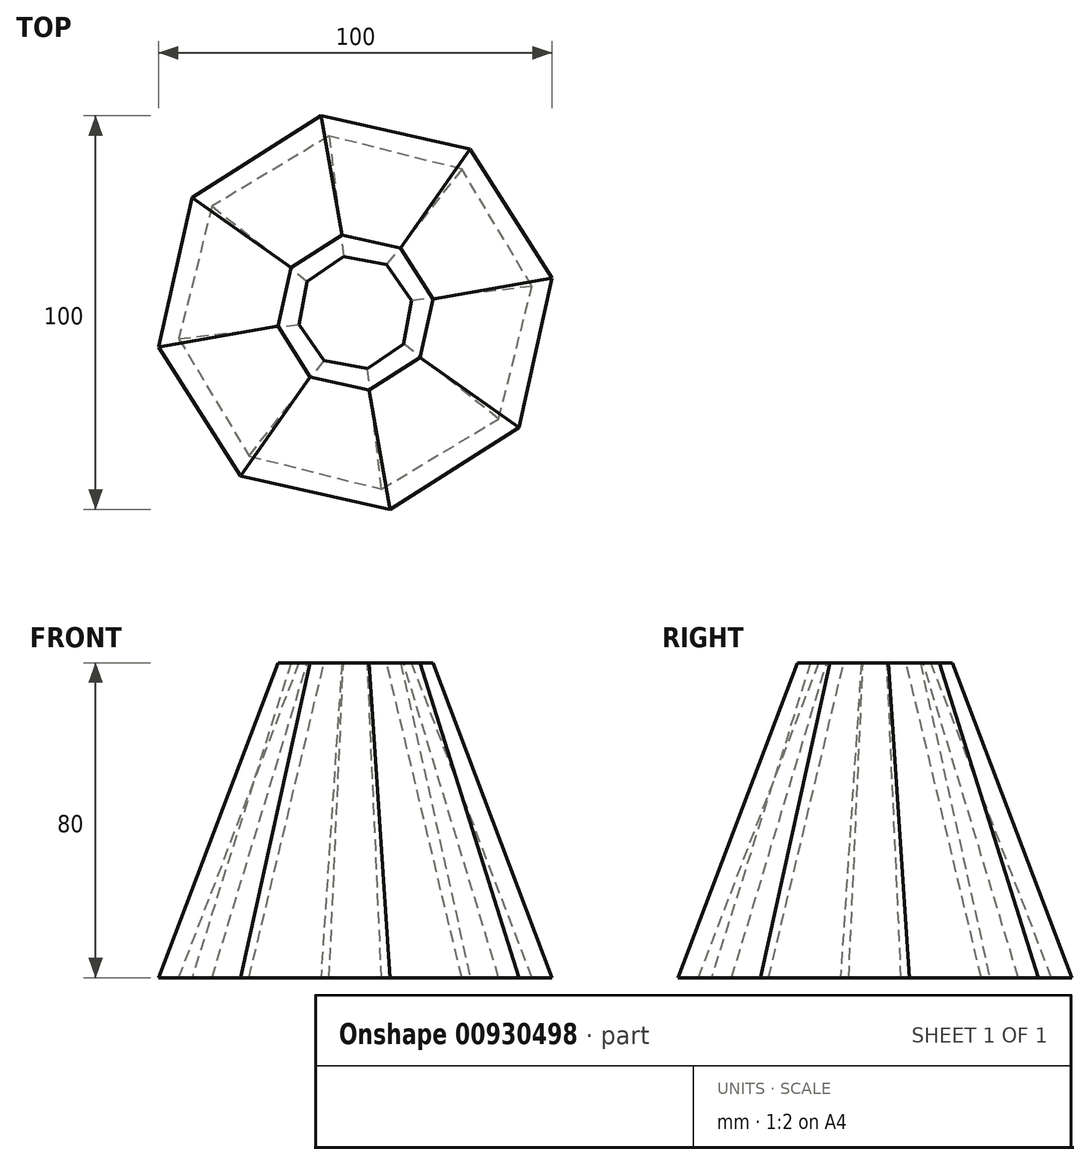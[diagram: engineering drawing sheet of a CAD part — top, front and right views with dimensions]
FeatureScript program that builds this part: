
annotation { "Feature Type Name" : "Feature", "Feature Type Description" : "" }
export const myFeature = defineFeature(function(context is Context, id is Id, definition is map)
    precondition{}
    {
        {
            var Q0;
            Q0=qCreatedBy(makeId("Top.planeOp"),FACE);
            var sketch = newSketch(context, id + "F0", { "sketchPlane" : qUnion([Q0])});
            skCircle(sketch, "E0.cCircle", {"center": v(0, 0) * mm, "radius": 46.9 * mm, "construction": true});
            skLineSegment(sketch, "E0.0", {"start": v(41.56, -29.15) * mm, "end": v(8.77, -50) * mm});
            skLineSegment(sketch, "E0.1", {"start": v(8.77, -50) * mm, "end": v(-29.15, -41.56) * mm});
            skLineSegment(sketch, "E0.2", {"start": v(-29.15, -41.56) * mm, "end": v(-50, -8.77) * mm});
            skLineSegment(sketch, "E0.3", {"start": v(-50, -8.77) * mm, "end": v(-41.56, 29.15) * mm});
            skLineSegment(sketch, "E0.4", {"start": v(-41.56, 29.15) * mm, "end": v(-8.77, 50) * mm});
            skLineSegment(sketch, "E0.5", {"start": v(-8.77, 50) * mm, "end": v(29.15, 41.56) * mm});
            skLineSegment(sketch, "E0.6", {"start": v(29.15, 41.56) * mm, "end": v(50, 8.77) * mm});
            skLineSegment(sketch, "E0.7", {"start": v(50, 8.77) * mm, "end": v(41.56, -29.15) * mm});
            skPoint(sketch, "E0.0.midPoint", {"position": v(25.16, -39.58) * mm});
            skPoint(sketch, "E1.0.midPoint", {"position": v(27.2, -39.24) * mm});
            skPoint(sketch, "E2.0.midPoint", {"position": v(4.46, -28.05) * mm});
            skCircle(sketch, "E3.cCircle", {"center": v(0, 0) * mm, "radius": 33.05 * mm, "construction": true});
            skLineSegment(sketch, "E3.0", {"start": v(29.09, -20.82) * mm, "end": v(5.85, -35.29) * mm});
            skLineSegment(sketch, "E3.1", {"start": v(5.85, -35.29) * mm, "end": v(-20.82, -29.09) * mm});
            skLineSegment(sketch, "E3.2", {"start": v(-20.82, -29.09) * mm, "end": v(-35.29, -5.85) * mm});
            skLineSegment(sketch, "E3.3", {"start": v(-35.29, -5.85) * mm, "end": v(-29.09, 20.82) * mm});
            skLineSegment(sketch, "E3.4", {"start": v(-29.09, 20.82) * mm, "end": v(-5.85, 35.29) * mm});
            skLineSegment(sketch, "E3.5", {"start": v(-5.85, 35.29) * mm, "end": v(20.82, 29.09) * mm});
            skLineSegment(sketch, "E3.6", {"start": v(20.82, 29.09) * mm, "end": v(35.29, 5.85) * mm});
            skLineSegment(sketch, "E3.7", {"start": v(35.29, 5.85) * mm, "end": v(29.09, -20.82) * mm});
            skPoint(sketch, "E3.0.midPoint", {"position": v(17.47, -28.05) * mm});
            skLineSegment(sketch, "E4", {"start": v(-8.77, 50) * mm, "end": v(-5.85, 35.29) * mm});
            skLineSegment(sketch, "E5", {"start": v(29.15, 41.56) * mm, "end": v(20.82, 29.09) * mm});
            skLineSegment(sketch, "E6", {"start": v(50, 8.77) * mm, "end": v(35.29, 5.85) * mm});
            skLineSegment(sketch, "E7", {"start": v(41.56, -29.15) * mm, "end": v(29.09, -20.82) * mm});
            skLineSegment(sketch, "E8", {"start": v(8.77, -50) * mm, "end": v(5.85, -35.29) * mm});
            skLineSegment(sketch, "E9", {"start": v(-29.15, -41.56) * mm, "end": v(-20.82, -29.09) * mm});
            skLineSegment(sketch, "E10", {"start": v(-50, -8.77) * mm, "end": v(-35.29, -5.85) * mm});
            skLineSegment(sketch, "E11", {"start": v(-41.56, 29.15) * mm, "end": v(-29.09, 20.82) * mm});
            skSolve(sketch);
        }
        {
            var Q0;
            Q0=makeQuery(id+"F0.imprint","IMPRINT",FACE,{"disambiguationData":[TD([[makeQuery(id+"F0.imprint","IMPRINT",EDGE,{"derivedFrom":sQuery(id+"F0.wireOp",EDGE,"E3.0")}),-1.0]])]});
            var Q1;
            Q1=makeQuery(id+"F0.imprint","IMPRINT",FACE,{"disambiguationData":[TD([[makeQuery(id+"F0.imprint","IMPRINT",EDGE,{"derivedFrom":sQuery(id+"F0.wireOp",EDGE,"E0.7")}),-1.0]])]});
            var Q2;
            Q2=makeQuery(id+"F0.imprint","IMPRINT",FACE,{"disambiguationData":[TD([[makeQuery(id+"F0.imprint","IMPRINT",EDGE,{"derivedFrom":sQuery(id+"F0.wireOp",EDGE,"E0.6")}),-1.0]])]});
            var Q3;
            Q3=makeQuery(id+"F0.imprint","IMPRINT",FACE,{"disambiguationData":[TD([[makeQuery(id+"F0.imprint","IMPRINT",EDGE,{"derivedFrom":sQuery(id+"F0.wireOp",EDGE,"E0.5")}),-1.0]])]});
            var Q4;
            Q4=makeQuery(id+"F0.imprint","IMPRINT",FACE,{"disambiguationData":[TD([[makeQuery(id+"F0.imprint","IMPRINT",EDGE,{"derivedFrom":sQuery(id+"F0.wireOp",EDGE,"E0.4")}),-1.0]])]});
            var Q5;
            Q5=makeQuery(id+"F0.imprint","IMPRINT",FACE,{"disambiguationData":[TD([[makeQuery(id+"F0.imprint","IMPRINT",EDGE,{"derivedFrom":sQuery(id+"F0.wireOp",EDGE,"E0.3")}),-1.0]])]});
            var Q6;
            Q6=makeQuery(id+"F0.imprint","IMPRINT",FACE,{"disambiguationData":[TD([[makeQuery(id+"F0.imprint","IMPRINT",EDGE,{"derivedFrom":sQuery(id+"F0.wireOp",EDGE,"E0.2")}),-1.0]])]});
            var Q7;
            Q7=makeQuery(id+"F0.imprint","IMPRINT",FACE,{"disambiguationData":[TD([[makeQuery(id+"F0.imprint","IMPRINT",EDGE,{"derivedFrom":sQuery(id+"F0.wireOp",EDGE,"E0.1")}),-1.0]])]});
            var Q8;
            Q8=makeQuery(id+"F0.imprint","IMPRINT",FACE,{"disambiguationData":[TD([[makeQuery(id+"F0.imprint","IMPRINT",EDGE,{"derivedFrom":sQuery(id+"F0.wireOp",EDGE,"E0.0")}),-1.0]])]});
            extrude(context, id + "F1", {"entities" : qUnion([Q0, Q1, Q2, Q3, Q4, Q5, Q6, Q7, Q8]), "depth" : 80 * mm, "offsetDistance" : 25 * mm});
        }
        {
            var Q0;
            Q0=makeQuery(id+"F1.opExtrude","CAP_FACE",FACE,{"disambiguationData":[OSD([sQuery(id+"F0.wireOp",EDGE,"E0.0"),sQuery(id+"F0.wireOp",EDGE,"E0.1"),sQuery(id+"F0.wireOp",EDGE,"E0.2"),sQuery(id+"F0.wireOp",EDGE,"E0.3"),sQuery(id+"F0.wireOp",EDGE,"E0.4"),sQuery(id+"F0.wireOp",EDGE,"E0.5"),sQuery(id+"F0.wireOp",EDGE,"E0.6"),sQuery(id+"F0.wireOp",EDGE,"E0.7")])],"isStart":false});
            var sketch = newSketch(context, id + "F2", { "sketchPlane" : qUnion([Q0])});
            skPoint(sketch, "E12.0.midPoint", {"position": v(11.44, -10.72) * mm});
            skCircle(sketch, "E13.cCircle", {"center": v(0, 0) * mm, "radius": 18.48 * mm, "construction": true});
            skLineSegment(sketch, "E13.0", {"start": v(16.37, -11.49) * mm, "end": v(3.46, -19.7) * mm});
            skLineSegment(sketch, "E13.1", {"start": v(3.46, -19.7) * mm, "end": v(-11.49, -16.37) * mm});
            skLineSegment(sketch, "E13.2", {"start": v(-11.49, -16.37) * mm, "end": v(-19.7, -3.46) * mm});
            skLineSegment(sketch, "E13.3", {"start": v(-19.7, -3.46) * mm, "end": v(-16.37, 11.49) * mm});
            skLineSegment(sketch, "E13.4", {"start": v(-16.37, 11.49) * mm, "end": v(-3.46, 19.7) * mm});
            skLineSegment(sketch, "E13.5", {"start": v(-3.46, 19.7) * mm, "end": v(11.49, 16.37) * mm});
            skLineSegment(sketch, "E13.6", {"start": v(11.49, 16.37) * mm, "end": v(19.7, 3.46) * mm});
            skLineSegment(sketch, "E13.7", {"start": v(19.7, 3.46) * mm, "end": v(16.37, -11.49) * mm});
            skPoint(sketch, "E13.0.midPoint", {"position": v(9.91, -15.6) * mm});
            skSolve(sketch);
        }
        {
            var Q1;
            Q1=makeQuery(id+"F2.imprint","IMPRINT",FACE,{"disambiguationData":[TD([[makeQuery(id+"F2.imprint","IMPRINT",EDGE,{"derivedFrom":sQuery(id+"F2.wireOp",EDGE,"E13.0")}),-1.0]])]});
            var Q2;
            Q2=makeQuery(id+"F1.opExtrude","CAP_FACE",FACE,{"disambiguationData":[OSD([sQuery(id+"F0.wireOp",EDGE,"E0.0"),sQuery(id+"F0.wireOp",EDGE,"E0.1"),sQuery(id+"F0.wireOp",EDGE,"E0.2"),sQuery(id+"F0.wireOp",EDGE,"E0.3"),sQuery(id+"F0.wireOp",EDGE,"E0.4"),sQuery(id+"F0.wireOp",EDGE,"E0.5"),sQuery(id+"F0.wireOp",EDGE,"E0.6"),sQuery(id+"F0.wireOp",EDGE,"E0.7")])],"isStart":true});
            loft(context, id + "F3", {"operationType" : NewBodyOperationType.INTERSECT, "surfaceOperationType" : NewSurfaceOperationType.ADD, "sheetProfilesArray" : [{ "sheetProfileEntities" : qUnion([Q1]) }, { "sheetProfileEntities" : qUnion([Q2]) }]});
        }
        {
            var Q0;
            Q0=makeQuery(id+"F1.opExtrude","CAP_FACE",FACE,{"disambiguationData":[OSD([sQuery(id+"F0.wireOp",EDGE,"E0.0"),sQuery(id+"F0.wireOp",EDGE,"E0.1"),sQuery(id+"F0.wireOp",EDGE,"E0.2"),sQuery(id+"F0.wireOp",EDGE,"E0.3"),sQuery(id+"F0.wireOp",EDGE,"E0.4"),sQuery(id+"F0.wireOp",EDGE,"E0.5"),sQuery(id+"F0.wireOp",EDGE,"E0.6"),sQuery(id+"F0.wireOp",EDGE,"E0.7")])],"isStart":false});
            var sketch = newSketch(context, id + "F4", { "sketchPlane" : qUnion([Q0])});
            skPoint(sketch, "E14.0.midPoint", {"position": v(12.65, -11.58) * mm});
            skCircle(sketch, "E15.cCircle", {"center": v(0, 0) * mm, "radius": 13.48 * mm, "construction": true});
            skLineSegment(sketch, "E15.0", {"start": v(12.24, -7.94) * mm, "end": v(3.04, -14.27) * mm});
            skLineSegment(sketch, "E15.1", {"start": v(3.04, -14.27) * mm, "end": v(-7.94, -12.24) * mm});
            skLineSegment(sketch, "E15.2", {"start": v(-7.94, -12.24) * mm, "end": v(-14.27, -3.04) * mm});
            skLineSegment(sketch, "E15.3", {"start": v(-14.27, -3.04) * mm, "end": v(-12.24, 7.94) * mm});
            skLineSegment(sketch, "E15.4", {"start": v(-12.24, 7.94) * mm, "end": v(-3.04, 14.27) * mm});
            skLineSegment(sketch, "E15.5", {"start": v(-3.04, 14.27) * mm, "end": v(7.94, 12.24) * mm});
            skLineSegment(sketch, "E15.6", {"start": v(7.94, 12.24) * mm, "end": v(14.27, 3.04) * mm});
            skLineSegment(sketch, "E15.7", {"start": v(14.27, 3.04) * mm, "end": v(12.24, -7.94) * mm});
            skPoint(sketch, "E15.0.midPoint", {"position": v(7.64, -11.1) * mm});
            skSolve(sketch);
        }
        {
            var Q0;
            Q0=makeQuery(id+"F1.opExtrude","CAP_FACE",FACE,{"disambiguationData":[OSD([sQuery(id+"F0.wireOp",EDGE,"E0.0"),sQuery(id+"F0.wireOp",EDGE,"E0.1"),sQuery(id+"F0.wireOp",EDGE,"E0.2"),sQuery(id+"F0.wireOp",EDGE,"E0.3"),sQuery(id+"F0.wireOp",EDGE,"E0.4"),sQuery(id+"F0.wireOp",EDGE,"E0.5"),sQuery(id+"F0.wireOp",EDGE,"E0.6"),sQuery(id+"F0.wireOp",EDGE,"E0.7")])],"isStart":true});
            var sketch = newSketch(context, id + "F5", { "sketchPlane" : qUnion([Q0])});
            skPoint(sketch, "E16.0.midPoint", {"position": v(-1.4, -34.44) * mm});
            skCircle(sketch, "E17.cCircle", {"center": v(0, 0) * mm, "radius": 41.9 * mm, "construction": true});
            skPoint(sketch, "E17.cCircle.perimeterSnap0", {"position": v(10.2, -45.78) * mm});
            skLineSegment(sketch, "E17.0", {"start": v(27.03, -36.42) * mm, "end": v(-6.64, -44.86) * mm});
            skLineSegment(sketch, "E17.1", {"start": v(-6.64, -44.86) * mm, "end": v(-36.42, -27.03) * mm});
            skLineSegment(sketch, "E17.2", {"start": v(-36.42, -27.03) * mm, "end": v(-44.86, 6.64) * mm});
            skLineSegment(sketch, "E17.3", {"start": v(-44.86, 6.64) * mm, "end": v(-27.03, 36.42) * mm});
            skLineSegment(sketch, "E17.4", {"start": v(-27.03, 36.42) * mm, "end": v(6.64, 44.86) * mm});
            skLineSegment(sketch, "E17.5", {"start": v(6.64, 44.86) * mm, "end": v(36.42, 27.03) * mm});
            skLineSegment(sketch, "E17.6", {"start": v(36.42, 27.03) * mm, "end": v(44.86, -6.64) * mm});
            skLineSegment(sketch, "E17.7", {"start": v(44.86, -6.64) * mm, "end": v(27.03, -36.42) * mm});
            skPoint(sketch, "E17.0.midPoint", {"position": v(10.2, -40.64) * mm});
            skPoint(sketch, "E17.0.midPoint.positionSnap0", {"position": v(10.2, -45.78) * mm});
            skSolve(sketch);
        }
        {
            var Q1;
            Q1=makeQuery(id+"F5.imprint","IMPRINT",FACE,{"disambiguationData":[TD([[makeQuery(id+"F5.imprint","IMPRINT",EDGE,{"derivedFrom":sQuery(id+"F5.wireOp",EDGE,"E17.0")}),-1.0]])]});
            var Q2;
            Q2=makeQuery(id+"F4.imprint","IMPRINT",FACE,{"disambiguationData":[TD([[makeQuery(id+"F4.imprint","IMPRINT",EDGE,{"derivedFrom":sQuery(id+"F4.wireOp",EDGE,"E15.0")}),-1.0]])]});
            loft(context, id + "F6", {"operationType" : NewBodyOperationType.REMOVE, "sheetProfilesArray" : [{ "sheetProfileEntities" : qUnion([Q1]) }, { "sheetProfileEntities" : qUnion([Q2]) }]});
        }
    });
